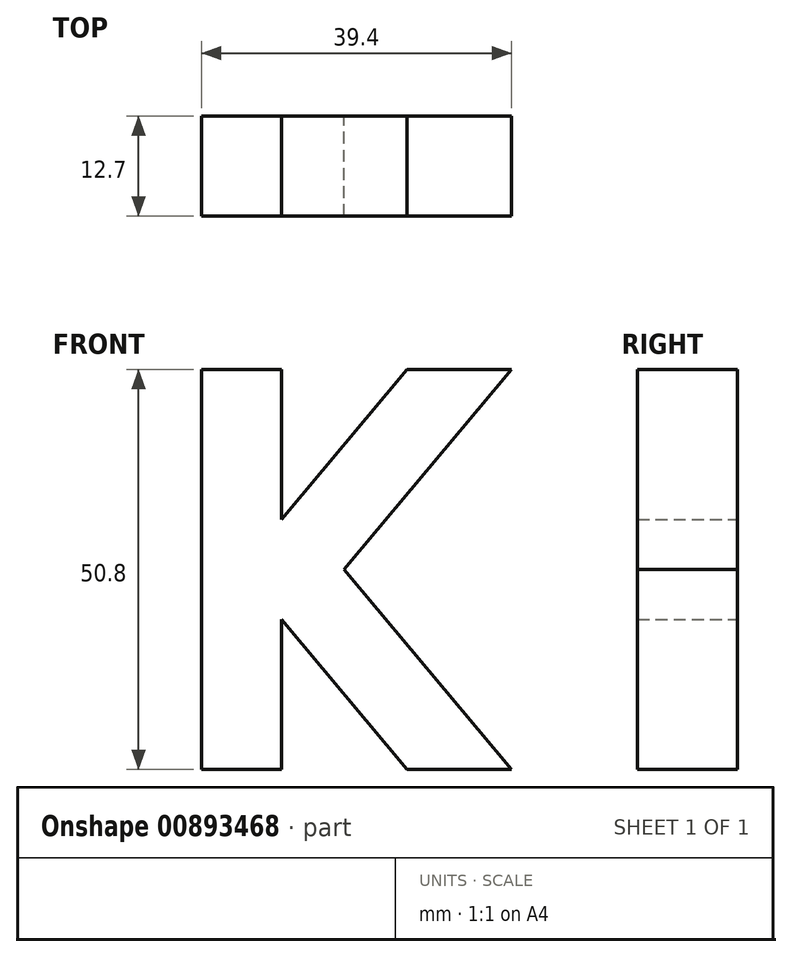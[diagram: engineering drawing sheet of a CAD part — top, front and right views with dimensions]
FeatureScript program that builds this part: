
annotation { "Feature Type Name" : "Feature", "Feature Type Description" : "" }
export const myFeature = defineFeature(function(context is Context, id is Id, definition is map)
    precondition{}
    {
        {
            var Q0;
            Q0=qCreatedBy(makeId("Front.planeOp"),FACE);
            var sketch = newSketch(context, id + "F0", { "sketchPlane" : qUnion([Q0])});
            skLineSegment(sketch, "E0", {"start": v(-18.1, 25.4) * mm, "end": v(-18.1, -25.4) * mm});
            skLineSegment(sketch, "E1", {"start": v(-18.1, -25.4) * mm, "end": v(-7.93, -25.4) * mm});
            skLineSegment(sketch, "E2", {"start": v(-7.93, -25.4) * mm, "end": v(-7.93, -6.35) * mm});
            skLineSegment(sketch, "E3", {"start": v(-7.93, -6.35) * mm, "end": v(8.05, -25.4) * mm});
            skLineSegment(sketch, "E4", {"start": v(8.05, -25.4) * mm, "end": v(21.31, -25.4) * mm});
            skLineSegment(sketch, "E5", {"start": v(21.31, -25.4) * mm, "end": v(0, 0) * mm});
            skLineSegment(sketch, "E6", {"start": v(0, 0) * mm, "end": v(21.31, 25.4) * mm});
            skLineSegment(sketch, "E7", {"start": v(21.31, 25.4) * mm, "end": v(8.05, 25.4) * mm});
            skLineSegment(sketch, "E8", {"start": v(8.05, 25.4) * mm, "end": v(-7.93, 6.35) * mm});
            skLineSegment(sketch, "E9", {"start": v(-7.93, 6.35) * mm, "end": v(-7.93, 25.4) * mm});
            skLineSegment(sketch, "E10", {"start": v(-7.93, 25.4) * mm, "end": v(-18.1, 25.4) * mm});
            skSolve(sketch);
        }
        {
            var Q0;
            Q0=makeQuery(id+"F0.imprint","IMPRINT",FACE,{"disambiguationData":[TD([[makeQuery(id+"F0.imprint","IMPRINT",EDGE,{"derivedFrom":sQuery(id+"F0.wireOp",EDGE,"E0")}),1.0]])]});
            extrude(context, id + "F1", {"entities" : qUnion([Q0]), "depth" : 12.7 * mm, "offsetDistance" : 25.4 * mm});
        }
    });
